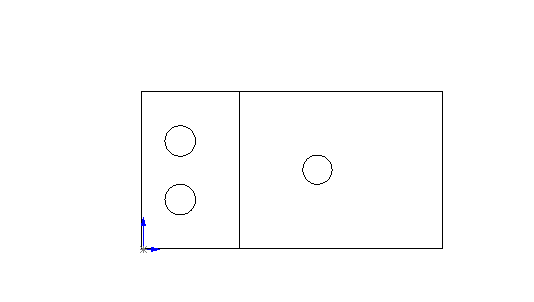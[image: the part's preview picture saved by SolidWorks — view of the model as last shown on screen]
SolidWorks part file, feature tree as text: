
SOLIDWORKS PART (.sldprt)
format: sldprt  version: not decoded by parser v0  size: 146,432 bytes
history: native  units: mm
features: sketch x4, cut_extrude x3, extrude x1 (+11 scaffold rows collapsed)
feature tree (19):
  scaffold x11  (default folders/planes/origin — collapsed)
  sketch  "Sketch1"  dims[D1=50.8mm D2=97.79mm]
  extrude  "Extrude2"  Depth=9.525mm
  sketch  "Sketch3"  dims[D1=38.1mm D2=57.15mm D3=31.75mm]
  cut_extrude  "Cut-Extrude1"  Depth=3.175mm
  sketch  "Sketch4"  dims[c1.D3=9.9314mm c1.D4=9.9314mm c1.D7=9.525mm c1.D1=25.4mm c1.D2=12.7mm c1.D5=9.2964mm c2.D1=18.9992mm c2.D6=25.4mm c2.D8=25.4mm c2.D9=25.4mm]
  cut_extrude  "Cut-Extrude2"  [1 undecoded]
  sketch  "Sketch5"  dims[D1=9.525mm D2=25.4mm D3=25.4mm]
  cut_extrude  "Cut-Extrude3"  [1 undecoded]
decode coverage: 6 of 8 modeling features carry decoded parameters
note: 2 parameter values undecoded
note: suppression state not decoded; provenance and decode notes live in map.json
